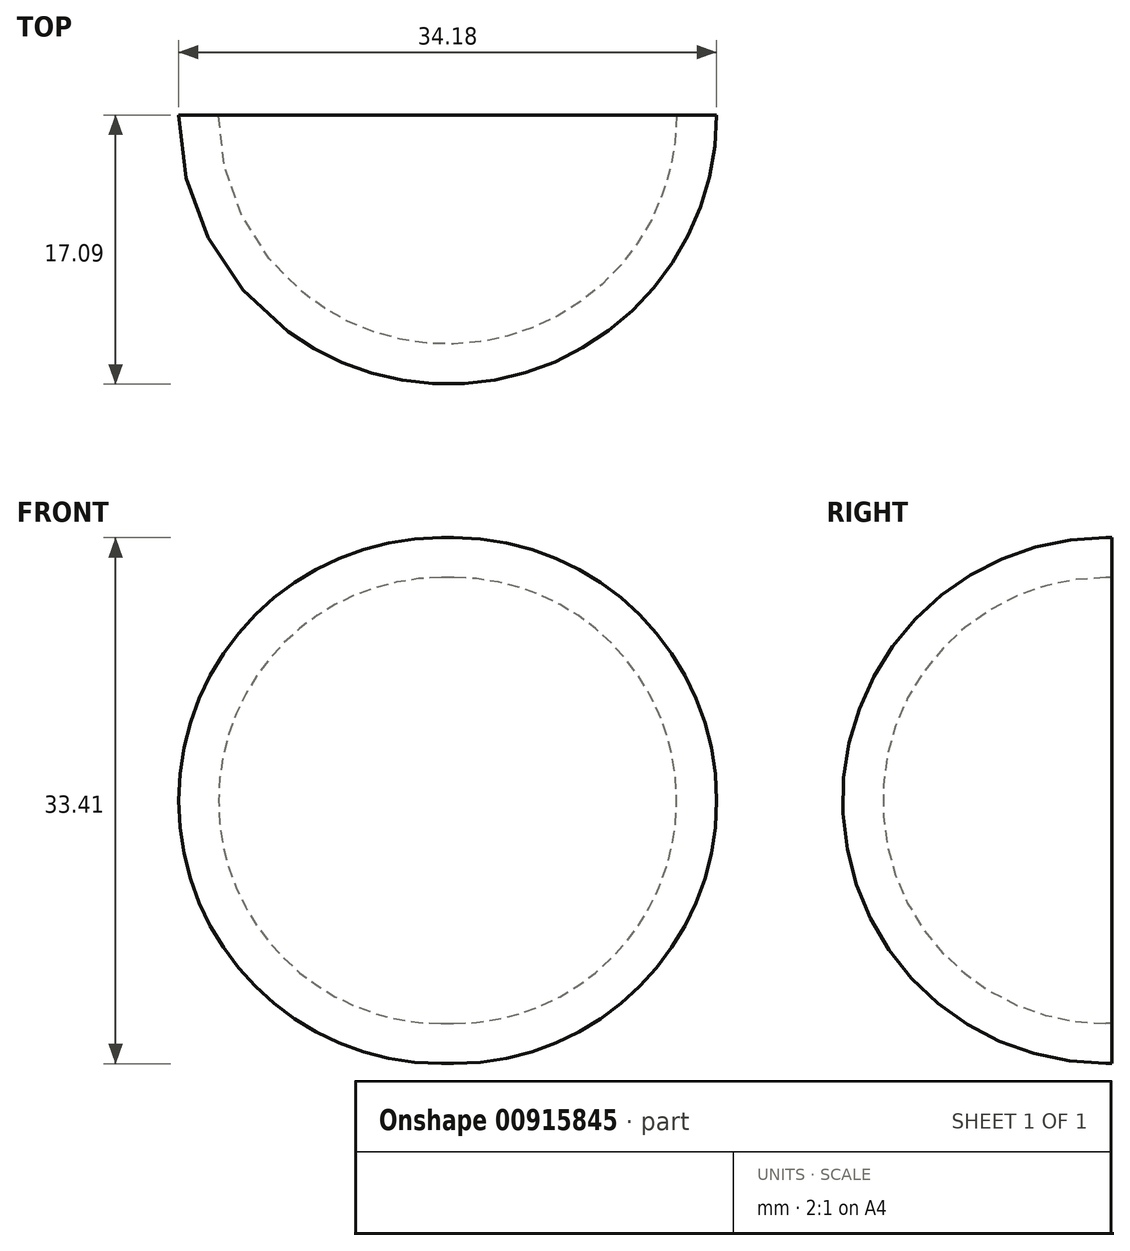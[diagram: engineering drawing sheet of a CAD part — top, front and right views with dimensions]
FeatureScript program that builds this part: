
annotation { "Feature Type Name" : "Feature", "Feature Type Description" : "" }
export const myFeature = defineFeature(function(context is Context, id is Id, definition is map)
    precondition{}
    {
        {
            var Q0;
            Q0=qCreatedBy(makeId("Front.planeOp"),FACE);
            var sketch = newSketch(context, id + "F0", { "sketchPlane" : qUnion([Q0])});
            skLineSegment(sketch, "E0", {"start": v(0, 55.23) * mm, "end": v(0, -55.23) * mm});
            skSolve(sketch);
        }
        {
            var Q0;
            Q0=qCreatedBy(makeId("Front.planeOp"),FACE);
            var sketch = newSketch(context, id + "F1", { "sketchPlane" : qUnion([Q0])});
            skArc(sketch, "E1", {"start": v(0, -15.28) * mm, "mid": v(17.09, 1.42) * mm, "end": v(0, 18.12) * mm});
            skLineSegment(sketch, "E2", {"start": v(0, 18.12) * mm, "end": v(0, -15.28) * mm});
            skSolve(sketch);
        }
        {
            var Q0;
            Q0=makeQuery(id+"F1.imprint","IMPRINT",FACE,{"disambiguationData":[TD([[makeQuery(id+"F1.imprint","IMPRINT",EDGE,{"derivedFrom":sQuery(id+"F1.wireOp",EDGE,"E1")}),1.0]])]});
            var Q1;
            Q1=sQuery(id+"F1.wireOp",EDGE,"E1");
            var Q2;
            Q2=sQuery(id+"F0.wireOp",EDGE,"E0");
            revolve(context, id + "F2", {"surfaceOperationType" : NewSurfaceOperationType.NEW, "entities" : qUnion([Q0]), "surfaceEntities" : qUnion([Q1]), "axis" : qUnion([Q2]), "revolveType" : RevolveType.ONE_DIRECTION, "angle" : 180 * degree});
        }
        {
            var Q0;
            Q0=makeQuery(id+"F2.opRevolve","CAP_FACE",FACE,{"disambiguationData":[OSD([sQuery(id+"F1.wireOp",EDGE,"E1"),sQuery(id+"F1.wireOp",EDGE,"E2")])],"isStart":true});
            var Q1;
            Q1=makeQuery(id+"F2.opRevolve","CAP_FACE",FACE,{"disambiguationData":[OSD([sQuery(id+"F1.wireOp",EDGE,"E1"),sQuery(id+"F1.wireOp",EDGE,"E2")])],"isStart":false});
            shell(context, id + "F3", {"entities" : qUnion([Q0, Q1]), "thickness" : 2.54 * mm});
        }
    });
